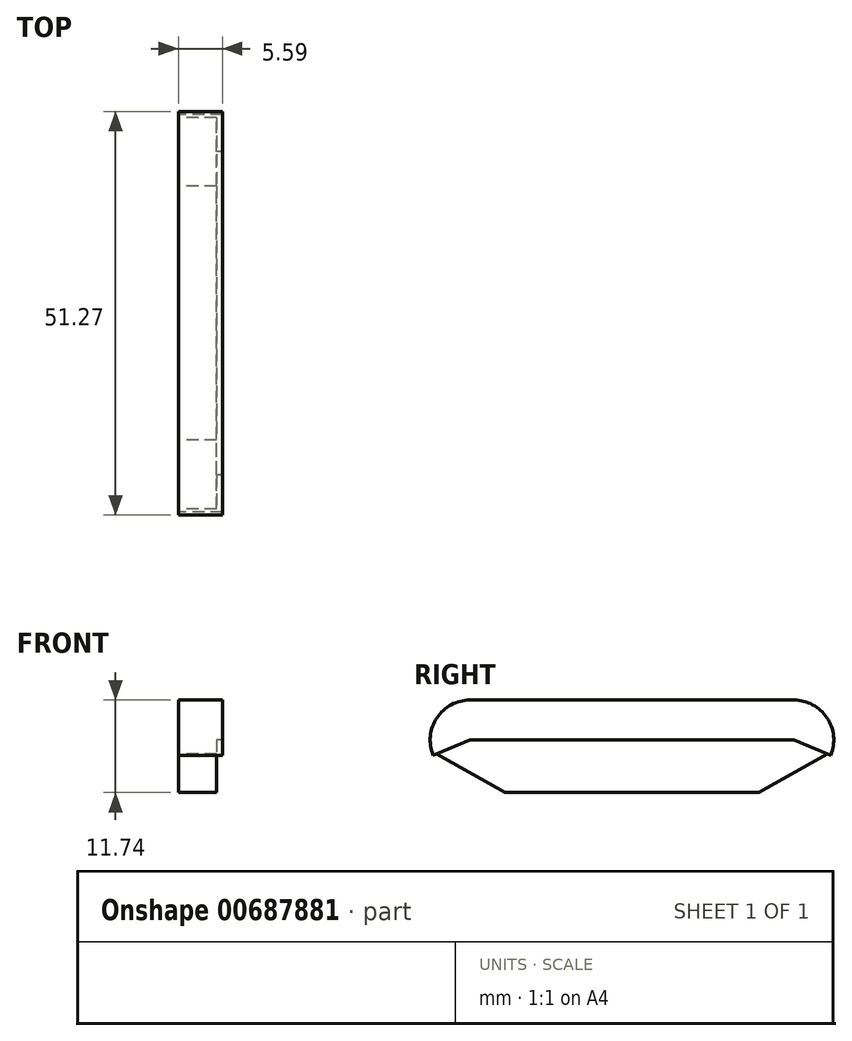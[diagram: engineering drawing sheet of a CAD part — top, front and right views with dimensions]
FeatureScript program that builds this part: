
annotation { "Feature Type Name" : "Feature", "Feature Type Description" : "" }
export const myFeature = defineFeature(function(context is Context, id is Id, definition is map)
    precondition{}
    {
        {
            var Q0;
            Q0=qCreatedBy(makeId("Right.planeOp"),FACE);
            var sketch = newSketch(context, id + "F0", { "sketchPlane" : qUnion([Q0])});
            skLineSegment(sketch, "E0", {"start": v(0, 0) * mm, "end": v(-20.56, 0) * mm});
            skLineSegment(sketch, "E1", {"start": v(0, 0) * mm, "end": v(20.57, 0) * mm});
            skLineSegment(sketch, "E2", {"start": v(-20.56, 0) * mm, "end": v(-20.56, -5.07) * mm});
            skLineSegment(sketch, "E3", {"start": v(-20.56, -5.07) * mm, "end": v(20.57, -5.07) * mm});
            skLineSegment(sketch, "E4", {"start": v(20.57, -5.07) * mm, "end": v(20.57, 0) * mm});
            skLineSegment(sketch, "E5", {"start": v(20.57, -5.07) * mm, "end": v(25.27, -7) * mm});
            skLineSegment(sketch, "E6", {"start": v(-20.56, -5.07) * mm, "end": v(-25.25, -7) * mm});
            skArc(sketch, "E7", {"start": v(-20.56, 0) * mm, "mid": v(-24.77, -2.25) * mm, "end": v(-25.25, -7) * mm});
            skArc(sketch, "E8", {"start": v(20.57, 0) * mm, "mid": v(24.79, -2.25) * mm, "end": v(25.26, -7) * mm});
            skLineSegment(sketch, "E9", {"start": v(-24.84, -6.83) * mm, "end": v(-16.12, -11.74) * mm});
            skLineSegment(sketch, "E10", {"start": v(24.86, -6.83) * mm, "end": v(16.14, -11.74) * mm});
            skLineSegment(sketch, "E11", {"start": v(16.14, -11.74) * mm, "end": v(-16.12, -11.74) * mm});
            skSolve(sketch);
        }
        {
            var Q0;
            {var subQ0=sQuery(id+"F0.wireOp",EDGE,"E2");Q0=makeQuery(id+"F0.imprint","IMPRINT",FACE,{"disambiguationData":[TD([[makeQuery(id+"F0.imprint","IMPRINT",EDGE,{"derivedFrom":subQ0}),-1.0]])]});}
            var Q1;
            Q1=makeQuery(id+"F0.imprint","IMPRINT",FACE,{"disambiguationData":[TD([[makeQuery(id+"F0.imprint","IMPRINT",EDGE,{"derivedFrom":sQuery(id+"F0.wireOp",EDGE,"E0")}),1.0]])]});
            var Q2;
            {var subQ0=sQuery(id+"F0.wireOp",EDGE,"E4");Q2=makeQuery(id+"F0.imprint","IMPRINT",FACE,{"disambiguationData":[TD([[makeQuery(id+"F0.imprint","IMPRINT",EDGE,{"derivedFrom":subQ0}),-1.0]])]});}
            extrude(context, id + "F1", {"entities" : qUnion([Q0, Q1, Q2]), "depth" : 5.6 * mm, "offsetDistance" : 25.4 * mm});
        }
        {
            var Q0;
            {var subQ2=sQuery(id+"F0.wireOp",EDGE,"E3");Q0=makeQuery(id+"F0.imprint","IMPRINT",FACE,{"disambiguationData":[TD([[makeQuery(id+"F0.imprint","IMPRINT",EDGE,{"derivedFrom":subQ2}),-1.0]])]});}
            extrude(context, id + "F2", {"entities" : qUnion([Q0]), "operationType" : NewBodyOperationType.ADD, "depth" : 4.83 * mm, "offsetDistance" : 25.4 * mm});
        }
    });
